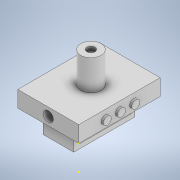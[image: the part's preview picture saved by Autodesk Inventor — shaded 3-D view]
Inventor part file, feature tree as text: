
AUTODESK INVENTOR PART (.ipt)
format: ipt  version: 2021 (Build 250183000, 183)  size: 212,992 bytes
history: native  units: mm
features: extrude x13, sketch x13, fillet x2
ambient origin geometry x8: Origin, YZ Plane, XZ Plane, XY Plane, X Axis, Y Axis, Z Axis, Center Point
bodies: Solid1 (feature_tree)
feature tree (28):
  extrude  "Extrusion1"  Depth=400.0mm
  sketch  "Sketch2"  dims[d2=300.0mm d3=0.0mm d4=40.0mm]
  extrude  "Extrusion2"  Depth=40.0mm
  extrude  "Extrusion3"  Depth=40.0mm
  extrude  "Extrusion4"  Depth=130.0mm
  extrude  "Extrusion5"  Depth=10.0mm TaperAngle=0.0deg
  extrude  "Extrusion6"  Depth=10.0mm TaperAngle=0.0deg
  sketch  "Sketch5"  dims[d9=70.0mm d10=10.0mm d11=0.0mm]
  sketch  "Sketch6"  dims[d12=10.0mm d13=0.0mm d14=10.0mm d15=0.0mm]
  extrude  "Extrusion7"  Depth=200.0mm
  extrude  "Extrusion8"  Depth=40.0mm
  sketch  "Sketch8"  dims[d18=150.0mm d19=0.0mm d20=40.0mm]
  extrude  "Extrusion9"  Depth=300.0mm
  extrude  "Extrusion10"  Depth=300.0mm
  extrude  "Extrusion11"  Depth=50.0mm
  fillet  "Fillet1"  Radius=100.0mm
  extrude  "Extrusion12"  Depth=150.0mm
  fillet  "Fillet2"  Radius=75.0mm
  extrude  "Extrusion13"  Depth=50.0mm
  sketch  "Sketch1"  dims[d0=80.0mm d1=400.0mm]
  sketch  "Sketch3"  dims[d5=40.0mm d6=40.0mm]
  sketch  "Sketch4"  dims[d7=130.0mm d8=130.0mm]
  sketch  "Sketch7"  dims[d16=100.0mm d17=200.0mm]
  sketch  "Sketch9"  dims[d21=20.0mm d22=0.0mm d23=300.0mm]
  sketch  "Sketch10"  dims[d24=150.0mm d25=300.0mm]
  sketch  "Sketch11"  dims[d26=75.0mm d27=50.0mm d28=100.0mm d29=0.0mm]
  sketch  "Sketch12"  dims[d30=60.0mm d31=150.0mm d32=75.0mm]
  sketch  "Sketch13"  dims[d33=20.0mm d34=0.0mm d35=50.0mm d36=150.0mm d37=40.0mm d38=50.0mm d39=0.0mm d40=50.0mm d41=0.0mm d42=250.0mm d43=60.0mm d44=10.0mm d45=0.0mm d46=4.0mm d47=350.0mm d48=40.0mm d49=10.0mm d50=0.0mm d51=2.0mm d52=40.0mm d53=100.0mm d54=0.0mm]
